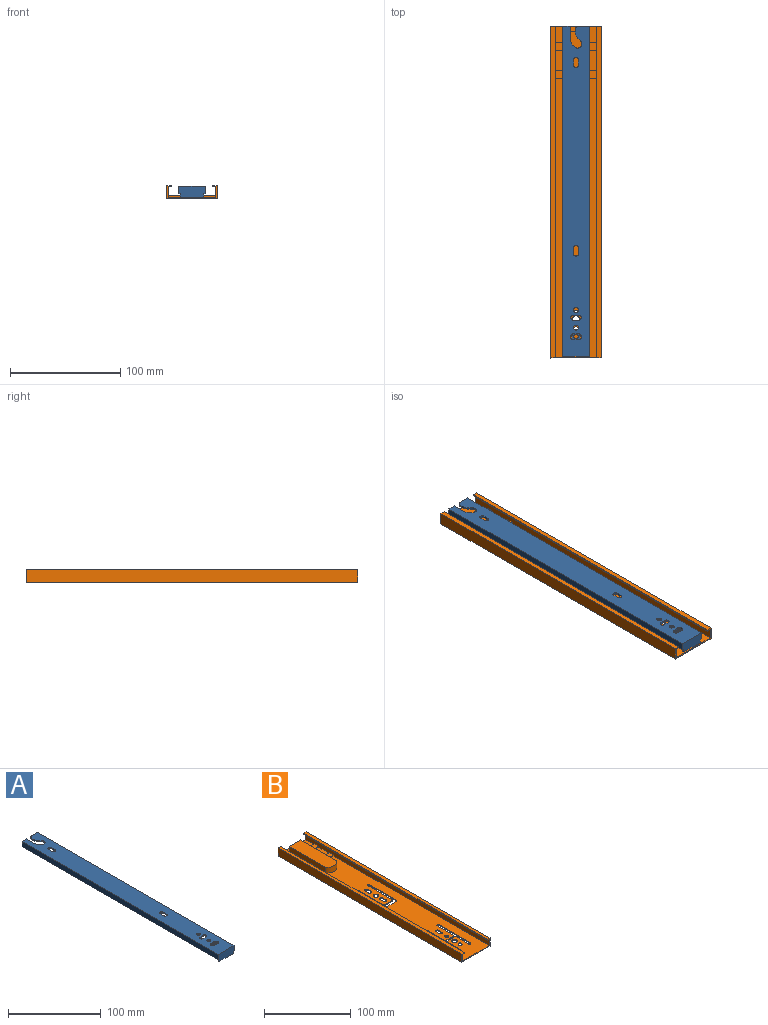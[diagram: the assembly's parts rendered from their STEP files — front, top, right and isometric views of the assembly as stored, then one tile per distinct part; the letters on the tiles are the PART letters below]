
ASSEMBLY  parts=2 mates=1
PART A: 54 faces, bbox 24.4x299x9.9 mm
  f0: plane 297.5x5.3mm, normal (-1,0,0), area 1576.7mm2, adj f39,f40,f43,f44
  f1: plane 5.1x1.5mm, normal (-1,0,0), area 7.6mm2, adj f2,f4,f37,f44
  f2: cylinder r=2.2mm len=4.4mm, axis (0,0,-1), area 10.4mm2, adj f1,f3,f37,f44
  f3: plane 5.1x1.5mm, normal (1,0,0), area 7.6mm2, adj f2,f4,f37,f44
  f4: cylinder r=2.2mm len=4.4mm, axis (0,0,-1), area 10.4mm2, adj f1,f3,f37,f44
  f5: plane 5.1x1.5mm, normal (-1,0,0), area 7.6mm2, adj f6,f8,f37,f44
  f6: cylinder r=2.2mm len=4.4mm, axis (0,0,-1), area 10.4mm2, adj f5,f7,f37,f44
  f7: plane 5.1x1.5mm, normal (1,0,0), area 7.6mm2, adj f6,f8,f37,f44
  f8: cylinder r=2.2mm len=4.4mm, axis (0,0,-1), area 10.4mm2, adj f5,f7,f37,f44
  f9: cylinder r=2.2mm len=4.4mm, axis (0,0,-1), area 10.4mm2, adj f10,f37,f44
  f10: cylinder r=2.2mm len=4.4mm, axis (0,0,-1), area 10.4mm2, adj f9,f37,f44
  f11: cylinder r=2.2mm len=4.4mm, axis (0,0,-1), area 10.4mm2, adj f12,f37,f44
  f12: cylinder r=2.2mm len=4.4mm, axis (0,0,-1), area 10.4mm2, adj f11,f37,f44
  f13: plane 5.1x1.5mm, normal (0,1,0), area 7.6mm2, adj f14,f16,f37,f44
  f14: cylinder r=2.2mm len=4.4mm, axis (0,0,-1), area 10.4mm2, adj f13,f15,f37,f44
  f15: plane 5.1x1.5mm, normal (0,-1,0), area 7.6mm2, adj f14,f16,f37,f44
  f16: cylinder r=2.2mm len=4.4mm, axis (0,0,-1), area 10.4mm2, adj f13,f15,f37,f44
  f17: cone r=2.1mm half-angle=45deg, axis (0,0,-1), area 2.5mm2, adj f18,f20,f50
  f18: cone r=2.1mm half-angle=45deg, axis (0,0,-1), area 2.5mm2, adj f17,f19,f50
  f19: cylinder r=2.1mm len=4.2mm, axis (0,0,1), area 5.6mm2, adj f18,f20,f24
  f20: cylinder r=2.1mm len=4.2mm, axis (0,0,1), area 5.6mm2, adj f17,f19,f24
  f21: plane 4.4x1.5mm, normal (0,-1,0), area 6.6mm2, adj f23,f24,f25,f37
  f22: plane 4.4x1.5mm, normal (0,1,0), area 6.6mm2, adj f23,f24,f25,f37
  f23: cylinder r=2.8mm len=5.6mm, axis (0,0,-1), area 13.2mm2, adj f21,f22,f24,f37,f44
  f24: plane 7.6x5.6mm, normal (0,0,1), area 25.8mm2, adj f19,f20,f21,f22,f23,f25,f45,f49
  f25: cylinder r=2.8mm len=5.6mm, axis (0,0,-1), area 13.2mm2, adj f21,f22,f24,f37,f44
  f26: plane 297.5x5.3mm, normal (1,0,0), area 1576.7mm2, adj f28,f33,f43,f44
  f27: plane 3.1x1.5mm, normal (-1,0,0), area 4.7mm2, adj f28,f35,f42,f43
  f28: plane 299x1.5mm, normal (0,0,-1), area 448.5mm2, adj f26,f27,f33,f34,f35
  f29: cylinder r=12.11mm len=9.54mm, axis (0,0,1), area 16.5mm2, adj f30,f37,f38,f44
  f30: cylinder r=3.75mm len=6.71mm, axis (0,0,-1), area 17.1mm2, adj f29,f31,f37,f44
  f31: cylinder r=9.95mm len=8.42mm, axis (0,0,-1), area 15.1mm2, adj f30,f32,f37,f44
  f32: plane 11x1.5mm, normal (1,0,0), area 16.5mm2, adj f31,f33,f37,f44
  f33: plane 7x6.8mm, normal (0,1,0), area 18.4mm2, adj f26,f28,f32,f34,f37,f44
  f34: plane 299x6.8mm, normal (-1,0,0), area 2033.2mm2, adj f28,f33,f35,f37
  f35: plane 24.4x9.9mm, normal (0,-1,0), area 232.3mm2, adj f27,f28,f34,f36,f37,f40,f41,f42
  f36: plane 299x6.8mm, normal (1,0,0), area 2033.2mm2, adj f35,f37,f39,f40
  f37: plane 299x24.4mm, normal (0,0,1), area 6978.5mm2, adj f1,f2,f3,f4,f5,f6,f7,f8
  f38: cylinder r=3.75mm len=3.75mm, axis (0,0,1), area 8.8mm2, adj f29,f37,f39,f44
  f39: plane 9.35x6.8mm, normal (0,1,0), area 22mm2, adj f0,f36,f37,f38,f40,f44
  f40: plane 299x1.5mm, normal (0,0,-1), area 448.5mm2, adj f0,f35,f36,f39,f41
  f41: plane 3.1x1.5mm, normal (1,0,0), area 4.7mm2, adj f35,f40,f42,f43
  f42: plane 21.4x1.5mm, normal (0,0,-1), area 32.1mm2, adj f27,f35,f41,f43
  f43: plane 21.4x8.4mm, normal (0,1,0), area 179.8mm2, adj f0,f26,f27,f41,f42,f44
  f44: plane 297.5x21.4mm, normal (0,0,-1), area 5981.5mm2, adj f0,f1,f2,f3,f4,f5,f6,f7
  f45: plane 9.76x2.6mm, normal (1,-0.06,0), area 20.6mm2, adj f24,f44,f46,f47,f48,f50,f51
  f46: cylinder r=3.2mm len=6.39mm, axis (0,0,1), area 25.1mm2, adj f44,f45,f47,f49
  f47: plane 9.52x7.19mm, normal (0,0,-1), area 51.5mm2, adj f45,f46,f48,f49
  f48: cylinder r=5mm len=7.19mm, axis (0,0,1), area 12mm2, adj f45,f47,f49,f50
  f49: plane 9.76x2.6mm, normal (-1,-0.06,0), area 20.6mm2, adj f24,f44,f46,f47,f48,f50,f53
  f50: plane 8.8x7.6mm, normal (0,0,-1), area 38.6mm2, adj f17,f18,f45,f48,f49,f51,f52,f53
  f51: cylinder r=3.8mm len=1.1mm, axis (0,0,1), area 0.3mm2, adj f24,f45,f50,f52
  f52: cylinder r=3.8mm len=7.6mm, axis (0,0,1), area 13.1mm2, adj f24,f44,f50,f51,f53
  f53: cylinder r=3.8mm len=1.1mm, axis (0,0,1), area 0.3mm2, adj f24,f49,f50,f52
PART B: 91 faces, bbox 45.8x300x11.5 mm
  f0: plane 12.43x1.4mm, normal (0,-1,0), area 17.4mm2, adj f1,f78,f81,f88
  f1: plane 12.43x7.2mm, normal (0,0,1), area 89.5mm2, adj f0,f2,f78,f81
  f2: plane 12.43x1.4mm, normal (0,1,0), area 17.4mm2, adj f1,f3,f78,f81
  f3: plane 17.5x12.43mm, normal (0,0,1), area 217.4mm2, adj f2,f78,f80,f81
  f4: plane 300x3.1mm, normal (0,0,-1), area 930mm2, adj f5,f68,f82,f83
  f5: plane 300x1.2mm, normal (1,0,0), area 360mm2, adj f4,f67,f68,f82
  f6: cylinder r=1.5mm len=1.5mm, axis (0,0,1), area 2.8mm2, adj f7,f25,f65,f88
  f7: cylinder r=1.5mm len=1.5mm, axis (0,0,1), area 2.8mm2, adj f6,f8,f65,f88
  f8: plane 51x1.2mm, normal (-1,0,0), area 61.2mm2, adj f7,f9,f65,f88
  f9: cylinder r=1.5mm len=1.5mm, axis (0,0,1), area 2.8mm2, adj f8,f10,f65,f88
  f10: cylinder r=1.5mm len=1.5mm, axis (0,0,1), area 2.8mm2, adj f9,f11,f65,f88
  f11: plane 26.46x1.2mm, normal (1,0,0), area 31.8mm2, adj f10,f12,f65,f88
  f12: cylinder r=1mm len=1.2mm, axis (0,0,-1), area 1.9mm2, adj f11,f13,f65,f88
  f13: plane 12.5x1.2mm, normal (0,-1,0), area 15mm2, adj f12,f14,f65,f88
  f14: cylinder r=1mm len=1.2mm, axis (0,0,-1), area 1.9mm2, adj f13,f15,f65,f88
  f15: plane 26.46x1.2mm, normal (-1,0,0), area 31.8mm2, adj f14,f16,f65,f88
  f16: cylinder r=1.5mm len=1.5mm, axis (0,0,1), area 2.8mm2, adj f15,f17,f65,f88
  f17: cylinder r=1.5mm len=1.5mm, axis (0,0,1), area 2.8mm2, adj f16,f18,f65,f88
  f18: plane 51x1.2mm, normal (1,0,0), area 61.2mm2, adj f17,f19,f65,f88
  f19: cylinder r=1.5mm len=1.5mm, axis (0,0,1), area 2.8mm2, adj f18,f20,f65,f88
  f20: cylinder r=1.5mm len=1.5mm, axis (0,0,1), area 2.8mm2, adj f19,f21,f65,f88
  f21: plane 20.34x1.2mm, normal (-1,0,0), area 24.4mm2, adj f20,f22,f65,f88
  f22: cylinder r=1mm len=1.2mm, axis (0,0,-1), area 1.9mm2, adj f21,f23,f65,f88
  f23: plane 12.5x1.2mm, normal (0,1,0), area 15mm2, adj f22,f24,f65,f88
  f24: cylinder r=1mm len=1.2mm, axis (0,0,-1), area 1.9mm2, adj f23,f25,f65,f88
  f25: plane 20.34x1.2mm, normal (1,0,0), area 24.4mm2, adj f6,f24,f65,f88
  f26: plane 4.9x1.2mm, normal (1,0,0), area 5.9mm2, adj f27,f29,f65,f88
  f27: cylinder r=2.3mm len=4.6mm, axis (0,0,1), area 8.7mm2, adj f26,f28,f65,f88
  f28: plane 4.9x1.2mm, normal (-1,0,0), area 5.9mm2, adj f27,f29,f65,f88
  f29: cylinder r=2.3mm len=4.6mm, axis (0,0,1), area 8.7mm2, adj f26,f28,f65,f88
  f30: plane 4.9x1.2mm, normal (-1,0,0), area 5.9mm2, adj f31,f33,f65,f88
  f31: cylinder r=2.3mm len=4.6mm, axis (0,0,1), area 8.7mm2, adj f30,f32,f65,f88
  f32: plane 4.9x1.2mm, normal (1,0,0), area 5.9mm2, adj f31,f33,f65,f88
  f33: cylinder r=2.3mm len=4.6mm, axis (0,0,1), area 8.7mm2, adj f30,f32,f65,f88
  f34: cylinder r=3.2mm len=6.4mm, axis (0,0,1), area 12.1mm2, adj f35,f65,f88
  f35: cylinder r=3.2mm len=6.4mm, axis (0,0,1), area 12.1mm2, adj f34,f65,f88
  f36: cylinder r=2.3mm len=4.6mm, axis (0,0,1), area 8.7mm2, adj f37,f65,f88
  f37: cylinder r=2.3mm len=4.6mm, axis (0,0,1), area 8.7mm2, adj f36,f65,f88
  f38: cylinder r=2.3mm len=4.6mm, axis (0,0,1), area 8.7mm2, adj f39,f65,f88
  f39: cylinder r=2.3mm len=4.6mm, axis (0,0,1), area 8.7mm2, adj f38,f65,f88
  f40: plane 4.6x4.6mm, normal (0,0,-1), area 16.6mm2, adj f41,f42
  f41: cylinder r=2.3mm len=4.6mm, axis (0,0,1), area 8.7mm2, adj f40,f42,f65
  f42: cylinder r=2.3mm len=4.6mm, axis (0,0,1), area 8.7mm2, adj f40,f41,f65
  f43: cylinder r=3.2mm len=6.4mm, axis (0,0,1), area 12.1mm2, adj f44,f65,f88
  f44: cylinder r=3.2mm len=6.4mm, axis (0,0,1), area 12.1mm2, adj f43,f65,f88
  f45: cylinder r=2.3mm len=4.6mm, axis (0,0,1), area 8.7mm2, adj f46,f48,f65,f88
  f46: plane 4.9x1.2mm, normal (1,0,0), area 5.9mm2, adj f45,f47,f65,f88
  f47: cylinder r=2.3mm len=4.6mm, axis (0,0,1), area 8.7mm2, adj f46,f48,f65,f88
  f48: plane 4.9x1.2mm, normal (-1,0,0), area 5.9mm2, adj f45,f47,f65,f88
  f49: plane 38.5x1.2mm, normal (1,0,0), area 46.2mm2, adj f50,f65,f88,f90
  f50: cylinder r=2mm len=2mm, axis (0,0,-1), area 3.8mm2, adj f49,f51,f65,f88
  f51: plane 10.5x1.2mm, normal (0,-1,0), area 12.6mm2, adj f50,f52,f65,f88
  f52: cylinder r=2mm len=2mm, axis (0,0,-1), area 3.8mm2, adj f51,f53,f65,f88
  f53: plane 38.5x1.2mm, normal (-1,0,0), area 46.2mm2, adj f52,f54,f65,f88
  f54: cylinder r=1.5mm len=1.5mm, axis (0,0,1), area 2.8mm2, adj f53,f55,f65,f88
  f55: cylinder r=1.5mm len=1.5mm, axis (0,0,1), area 2.8mm2, adj f54,f56,f65,f88
  f56: plane 42x1.2mm, normal (1,0,0), area 50.4mm2, adj f55,f57,f65,f88
  f57: cylinder r=3mm len=3mm, axis (0,0,1), area 5.7mm2, adj f56,f58,f65,f88
  f58: plane 14.5x1.2mm, normal (0,1,0), area 17.4mm2, adj f57,f59,f65,f88
  f59: cylinder r=3mm len=3mm, axis (0,0,1), area 5.7mm2, adj f58,f60,f65,f88
  f60: plane 42x1.2mm, normal (-1,0,0), area 50.4mm2, adj f59,f65,f88,f89
  f61: plane 300x3.1mm, normal (0,0,-1), area 930mm2, adj f62,f68,f81,f82
  f62: plane 300x1.2mm, normal (-1,0,0), area 360mm2, adj f61,f63,f68,f82
  f63: plane 300x4.3mm, normal (0,0,1), area 1290mm2, adj f62,f64,f68,f82
  f64: plane 300x11.5mm, normal (1,0,0), area 3450mm2, adj f63,f65,f68,f82
  f65: plane 300x45.75mm, normal (0,0,-1), area 12800.3mm2, adj f6,f7,f8,f9,f10,f11,f12,f13
  f66: plane 300x11.5mm, normal (-1,0,0), area 3450mm2, adj f65,f67,f68,f82
  f67: plane 300x4.3mm, normal (0,0,1), area 1290mm2, adj f5,f66,f68,f82
  f68: plane 45.75x11.5mm, normal (0,1,0), area 87.1mm2, adj f4,f5,f61,f62,f63,f64,f65,f66
  f69: plane 17.5x12.43mm, normal (0,0,1), area 217.4mm2, adj f70,f83,f84,f85
  f70: plane 12.43x1.4mm, normal (0,-1,0), area 17.4mm2, adj f69,f71,f83,f85
  f71: plane 12.43x7.2mm, normal (0,0,1), area 89.5mm2, adj f70,f72,f83,f85
  f72: plane 12.43x1.4mm, normal (0,1,0), area 17.4mm2, adj f71,f76,f83,f85
  f73: cylinder r=11.76mm len=18.5mm, axis (0,0,-1), area 170.3mm2, adj f74,f78,f85,f88
  f74: plane 63.5x18.5mm, normal (0,0,1), area 1149.5mm2, adj f73,f75,f78,f85
  f75: plane 18.5x8mm, normal (0,1,0), area 148mm2, adj f74,f76,f78,f85
  f76: plane 43.35x14.7mm, normal (0,0,1), area 455.9mm2, adj f68,f72,f75,f77,f78,f81,f83,f85
  f77: plane 12.43x1.4mm, normal (0,1,0), area 17.4mm2, adj f76,f78,f79,f81
  f78: plane 59x8mm, normal (1,0,0), area 451.8mm2, adj f0,f1,f2,f3,f73,f74,f75,f76
  f79: plane 12.43x7.2mm, normal (0,0,1), area 89.5mm2, adj f77,f78,f80,f81
  f80: plane 12.43x1.4mm, normal (0,-1,0), area 17.4mm2, adj f3,f78,f79,f81
  f81: plane 300x9.1mm, normal (-1,0,0), area 2709.8mm2, adj f0,f1,f2,f3,f61,f68,f76,f77
  f82: plane 45.75x11.5mm, normal (0,-1,0), area 87.1mm2, adj f4,f5,f61,f62,f63,f64,f65,f66
  f83: plane 300x9.1mm, normal (1,0,0), area 2709.8mm2, adj f4,f68,f69,f70,f71,f72,f76,f82
  f84: plane 12.43x1.4mm, normal (0,1,0), area 17.4mm2, adj f69,f83,f85,f86
  f85: plane 59x8mm, normal (-1,0,0), area 451.8mm2, adj f69,f70,f71,f72,f73,f74,f75,f76
  f86: plane 12.43x7.2mm, normal (0,0,1), area 89.5mm2, adj f83,f84,f85,f87
  f87: plane 12.43x1.4mm, normal (0,-1,0), area 17.4mm2, adj f83,f85,f86,f88
  f88: plane 253.4x43.35mm, normal (0,0,1), area 9698.7mm2, adj f0,f6,f7,f8,f9,f10,f11,f12
  f89: cylinder r=1.5mm len=1.5mm, axis (0,0,1), area 2.8mm2, adj f60,f65,f88,f90
  f90: cylinder r=1.5mm len=1.5mm, axis (0,0,1), area 2.8mm2, adj f49,f65,f88,f89
PLACE A rot(axis=(-0.11,-0.07,0.99),0deg) t=(128.82,287.22,-84.21)mm
PLACE B rot(axis=(-0.11,-0.07,0.99),0deg) t=(128.82,-0.28,-82.41)mm
MATE slider B.f75 <-> A.f43  axis (0,1,0) through (64.76,-5.18,-82.71)mm
